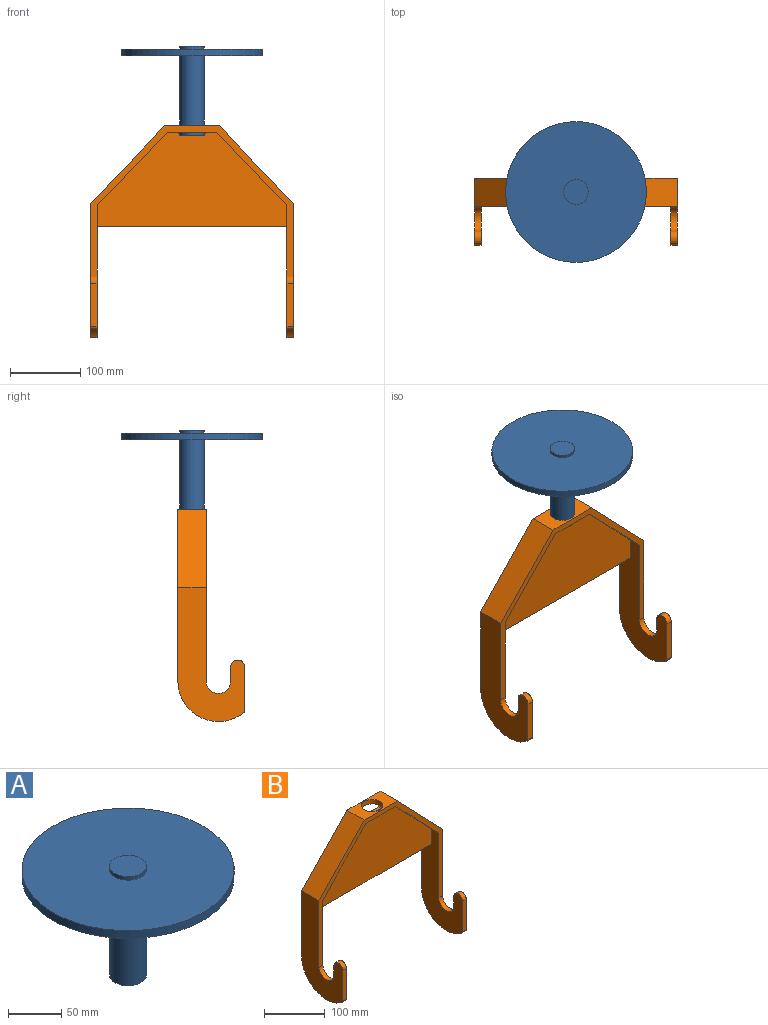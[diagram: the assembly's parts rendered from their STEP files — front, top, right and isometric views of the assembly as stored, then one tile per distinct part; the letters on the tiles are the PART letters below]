
ASSEMBLY  parts=2 mates=1
PART A: 7 faces, bbox 200x200x126 mm
  f0: cylinder r=17.5mm len=113mm, axis (0,0,1), area 12425mm2, adj f1,f6
  f1: plane 35x35mm, normal (0,0,-1), area 962.1mm2, adj f0
  f2: plane 35x35mm, normal (0,0,1), area 962.1mm2, adj f3
  f3: cylinder r=17.5mm len=35mm, axis (0,0,1), area 439.8mm2, adj f2,f4
  f4: plane 200x200mm, normal (0,0,1), area 30453.8mm2, adj f3,f5
  f5: cylinder r=100mm len=200mm, axis (0,0,1), area 5654.9mm2, adj f4,f6
  f6: plane 200x200mm, normal (0,0,-1), area 30453.8mm2, adj f0,f5
PART B: 33 faces, bbox 288x95x300.8 mm
  f0: plane 104.32x100mm, normal (0.72,0,-0.69), area 2456.7mm2, adj f2,f5,f14,f32
  f1: plane 104.32x100mm, normal (-0.72,0,-0.69), area 2456.7mm2, adj f2,f3,f14,f32
  f2: plane 70x40mm, normal (0,0,-1), area 1675.9mm2, adj f0,f1,f6,f7,f14,f23,f26,f28
  f3: plane 187.5x95mm, normal (-1,0,0), area 9683.7mm2, adj f1,f7,f12,f14,f17,f18,f20,f22
  f4: plane 191.12x95mm, normal (-1,0,0), area 10008.4mm2, adj f11,f13,f14,f15,f16,f19,f21,f23
  f5: plane 187.5x95mm, normal (1,0,0), area 9683.7mm2, adj f0,f6,f13,f14,f15,f16,f19,f21
  f6: plane 104.32x100mm, normal (0.72,0,-0.69), area 2456.7mm2, adj f2,f5,f23,f31
  f7: plane 104.32x100mm, normal (-0.72,0,-0.69), area 2456.7mm2, adj f2,f3,f23,f31
  f8: plane 191.12x95mm, normal (1,0,0), area 10008.4mm2, adj f9,f12,f14,f17,f18,f20,f22,f23
  f9: plane 109.7x105.16mm, normal (0.72,0,0.69), area 6078.6mm2, adj f8,f10,f14,f23
  f10: plane 77.68x40mm, normal (0,0,1), area 2145.1mm2, adj f9,f11,f14,f23,f26
  f11: plane 109.7x105.16mm, normal (-0.72,0,0.69), area 6078.6mm2, adj f4,f10,f14,f23
  f12: plane 61.23x9mm, normal (0,-1,0), area 551.1mm2, adj f3,f8,f18,f25
  f13: plane 61.23x9mm, normal (0,-1,0), area 551.1mm2, adj f4,f5,f16,f24
  f14: plane 288x243.32mm, normal (0,1,0), area 5705.4mm2, adj f0,f1,f2,f3,f4,f5,f8,f9
  f15: cylinder r=57.5mm len=93.1mm, axis (-1,0,0), area 1158.3mm2, adj f4,f5,f14,f16
  f16: cylinder r=5mm len=9mm, axis (-1,0,0), area 40.6mm2, adj f4,f5,f13,f15
  f17: cylinder r=57.5mm len=93.1mm, axis (-1,0,0), area 1158.3mm2, adj f3,f8,f14,f18
  f18: cylinder r=5mm len=9mm, axis (-1,0,0), area 40.6mm2, adj f3,f8,f12,f17
  f19: cylinder r=17.5mm len=35mm, axis (-1,0,0), area 494.8mm2, adj f4,f5,f21,f23
  f20: cylinder r=17.5mm len=35mm, axis (-1,0,0), area 494.8mm2, adj f3,f8,f22,f23
  f21: plane 20x9mm, normal (0,1,0), area 180mm2, adj f4,f5,f19,f24
  f22: plane 20x9mm, normal (0,1,0), area 180mm2, adj f3,f8,f20,f25
  f23: plane 288x243.32mm, normal (0,-1,0), area 5705.4mm2, adj f2,f3,f4,f5,f6,f7,f8,f9
  f24: cylinder r=10mm len=20mm, axis (-1,0,0), area 282.7mm2, adj f4,f5,f13,f21
  f25: cylinder r=10mm len=20mm, axis (-1,0,0), area 282.7mm2, adj f3,f8,f12,f22
  f26: cylinder r=17.5mm len=35mm, axis (0,0,1), area 989.6mm2, adj f2,f10
  f27: plane 270x6mm, normal (0,0,-1), area 1620mm2, adj f3,f5,f31,f32
  f28: plane 6x4mm, normal (-0.71,0,0.71), area 33.9mm2, adj f2,f29,f31,f32
  f29: plane 35x6mm, normal (0,0,1), area 210mm2, adj f28,f30,f31,f32
  f30: plane 6x4mm, normal (0.71,0,0.71), area 33.9mm2, adj f2,f29,f31,f32
  f31: plane 270x134.32mm, normal (0,-1,0), area 25678.6mm2, adj f2,f3,f5,f6,f7,f27,f28,f29
  f32: plane 270x134.32mm, normal (0,1,0), area 25678.6mm2, adj f0,f1,f2,f3,f5,f27,f28,f29
PLACE A t=(149.01,150.52,177.73)mm
PLACE B t=(31.51,170.52,-110.09)mm fixed
MATE fastened A.f0 <-> B.f26  axis (0,0,-1) through (166.51,150.52,177.73)mm
